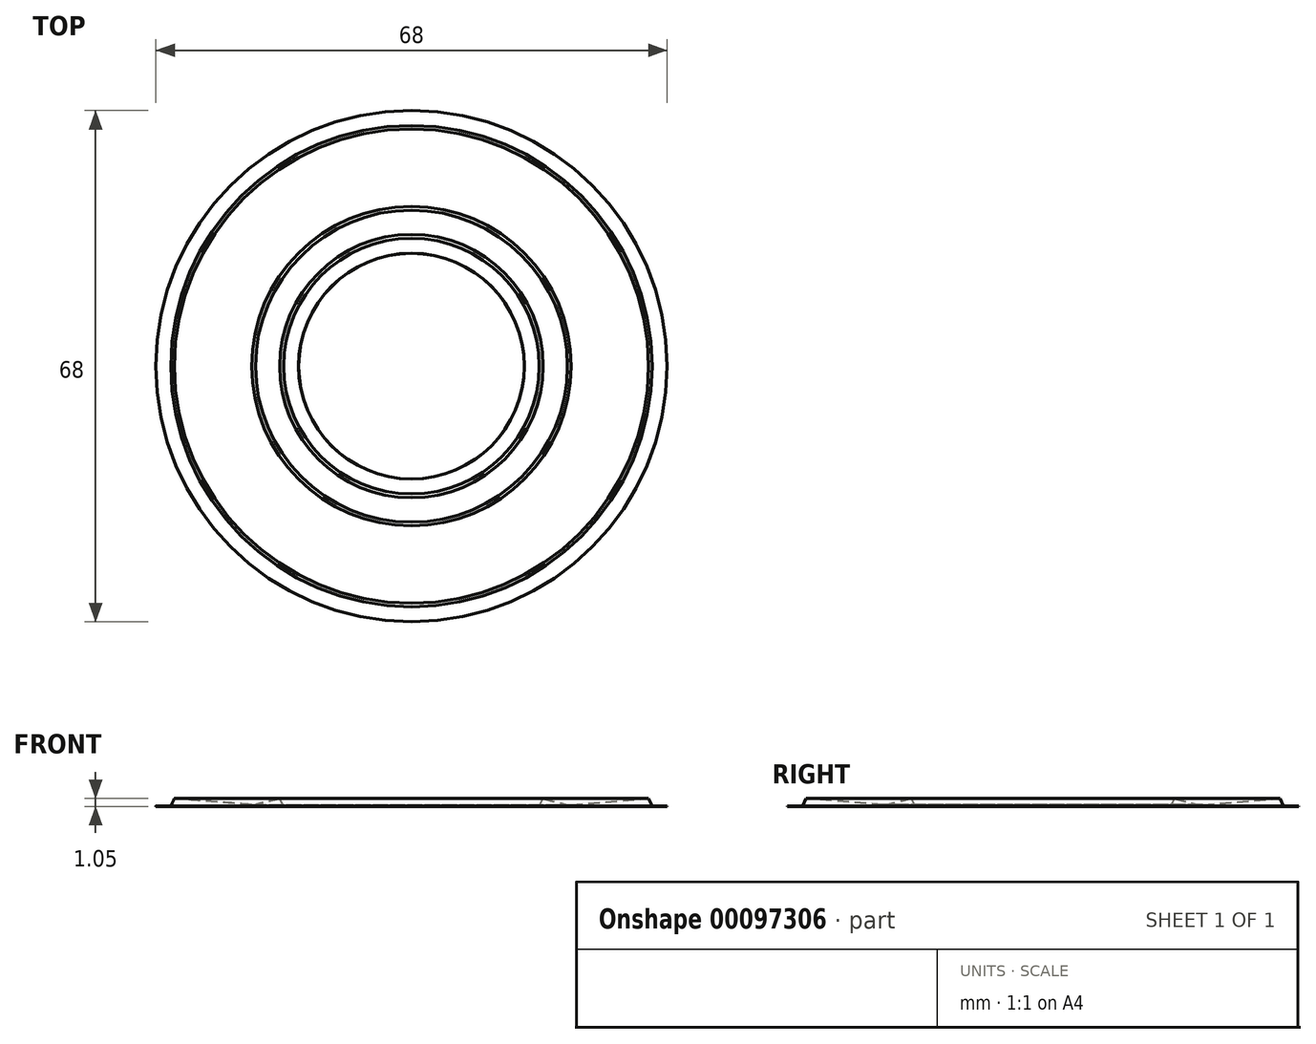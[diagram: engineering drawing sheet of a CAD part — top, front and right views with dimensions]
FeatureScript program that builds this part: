
annotation { "Feature Type Name" : "Feature", "Feature Type Description" : "" }
export const myFeature = defineFeature(function(context is Context, id is Id, definition is map)
    precondition{}
    {
        {
            var Q0;
            Q0=qCreatedBy(makeId("Front.planeOp"),FACE);
            var sketch = newSketch(context, id + "F0", { "sketchPlane" : qUnion([Q0])});
            skPoint(sketch, "E0", {"position": v(15, 0) * mm});
            skPoint(sketch, "E1", {"position": v(34, 0) * mm});
            skPoint(sketch, "E2", {"position": v(32, 0) * mm});
            skPoint(sketch, "E3", {"position": v(17, 0) * mm});
            skPoint(sketch, "E4", {"position": v(31.54, 1) * mm});
            skPoint(sketch, "E5", {"position": v(17.52, 1) * mm});
            skLineSegment(sketch, "E6", {"start": v(32, 0) * mm, "end": v(31.54, 1) * mm});
            skLineSegment(sketch, "E7", {"start": v(34, 0) * mm, "end": v(32, 0) * mm});
            skLineSegment(sketch, "E8", {"start": v(17, 0) * mm, "end": v(17.52, 1) * mm});
            skLineSegment(sketch, "E9", {"start": v(17, 0) * mm, "end": v(15, 0) * mm});
            skPoint(sketch, "E10", {"position": v(20.75, 0.2) * mm});
            skPoint(sketch, "E11", {"position": v(21.25, 0) * mm});
            skPoint(sketch, "E12", {"position": v(21.25, 0.2) * mm});
            skLineSegment(sketch, "E13", {"start": v(20.75, 0.2) * mm, "end": v(21.25, 0.2) * mm});
            skLineSegment(sketch, "E14", {"start": v(20.75, 0.2) * mm, "end": v(17.52, 1) * mm});
            skLineSegment(sketch, "E15", {"start": v(21.25, 0.2) * mm, "end": v(31.54, 1) * mm});
            skLineSegment(sketch, "E16", {"start": v(31.54, 1.05) * mm, "end": v(21.25, 0.25) * mm});
            skLineSegment(sketch, "E17", {"start": v(21.25, 0.25) * mm, "end": v(20.75, 0.25) * mm});
            skLineSegment(sketch, "E18", {"start": v(20.75, 0.25) * mm, "end": v(17.51, 1.05) * mm});
            skLineSegment(sketch, "E19", {"start": v(17.51, 1.05) * mm, "end": v(17, 0.05) * mm});
            skLineSegment(sketch, "E20", {"start": v(17, 0.05) * mm, "end": v(15.01, 0.05) * mm});
            skLineSegment(sketch, "E21", {"start": v(31.54, 1.05) * mm, "end": v(32, 0.05) * mm});
            skLineSegment(sketch, "E22", {"start": v(32, 0.05) * mm, "end": v(34, 0.05) * mm});
            skLineSegment(sketch, "E23", {"start": v(15.01, 0.05) * mm, "end": v(15, 0) * mm});
            skLineSegment(sketch, "E24", {"start": v(34, 0.05) * mm, "end": v(34, 0) * mm});
            skLineSegment(sketch, "E25", {"start": v(0, 0) * mm, "end": v(0, 10.39) * mm});
            skSolve(sketch);
        }
        {
            var Q0;
            Q0=makeQuery(id+"F0.imprint","IMPRINT",FACE,{"disambiguationData":[TD([[makeQuery(id+"F0.imprint","IMPRINT",EDGE,{"derivedFrom":sQuery(id+"F0.wireOp",EDGE,"E6")}),-1.0]])]});
            var Q1;
            Q1=sQuery(id+"F0.wireOp",EDGE,"E25");
            revolve(context, id + "F1", {"entities" : qUnion([Q0]), "axis" : qUnion([Q1]), "revolveType" : RevolveType.FULL});
        }
    });
